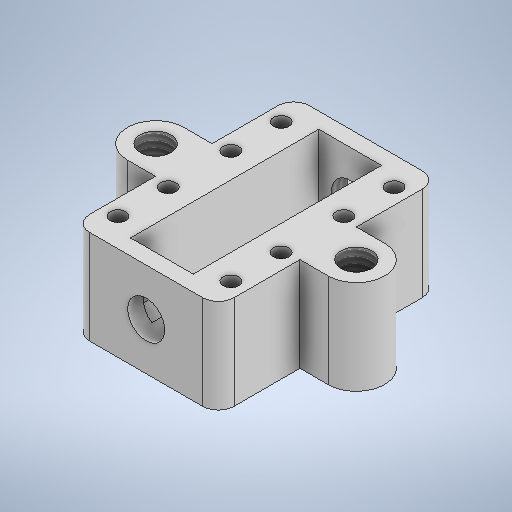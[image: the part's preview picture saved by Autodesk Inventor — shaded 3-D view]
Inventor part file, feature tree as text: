
AUTODESK INVENTOR PART (.ipt)
format: ipt  version: 2025.1 (Build 291241000, 241)  size: 332,800 bytes
history: native  units: mm
features: sketch x5, hole x3, extrude x2, mirror x1, fillet x1
ambient origin geometry x8: Origin, YZ Plane, XZ Plane, XY Plane, X Axis, Y Axis, Z Axis, Center Point
bodies: Solid1 (feature_tree)
feature tree (12):
  extrude  "Extrusion1"  Depth=23.0mm
  hole  "Hole1"  [1 undecoded]
  hole  "Hole2"  [1 undecoded]
  extrude  "Extrusion2"  Depth=16.0mm
  hole  "Hole3"  [1 undecoded]
  mirror  "Mirror1"
  fillet  "Fillet1"  Radius=30.0mm
  sketch  "Sketch1"  dims[d0=35.0mm d1=23.0mm]
  sketch  "Sketch2"  dims[d2=4.5mm d3=9.0mm]
  sketch  "Sketch3"  dims[d4=4.5mm d5=9.0mm]
  sketch  "Sketch4"  dims[d6=32.0mm d7=16.0mm]
  sketch  "Sketch6"  dims[d8=15.0mm d9=0.0mm d10=4.917mm d11=12.0mm d12=4.0mm d13=2.0mm d14=90.0deg d15=8.0mm d16=0.0mm d17=10.0mm d18=30.0mm d19=10.0mm d20=0.0mm d21=5.917468mm d22=14.0mm d23=4.0mm d24=2.0mm d25=90.0deg d26=8.0mm d27=0.0mm d31=8.0mm d35=2.5mm d36=2.5mm d37=4.0mm d38=2.0mm d39=90.0deg d40=8.0mm d41=0.0mm d42=5.0mm d43=18.0mm d44=9.0mm d45=2.5mm]
note: 3 required parameter values undecoded (feature->parameter linkage not recoverable at this tier; creation-order binding heuristic only, values carry confidence <= 0.55)
